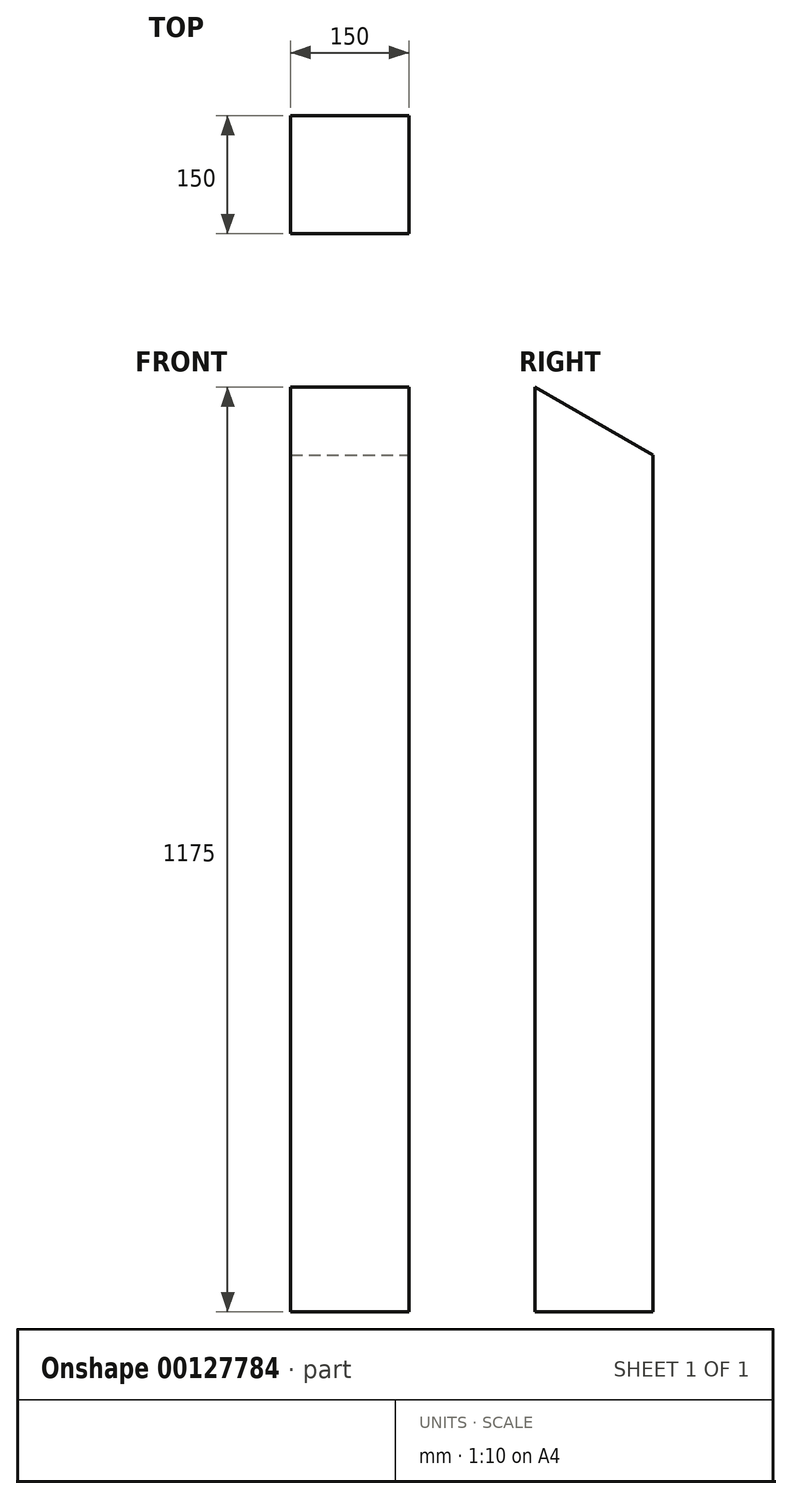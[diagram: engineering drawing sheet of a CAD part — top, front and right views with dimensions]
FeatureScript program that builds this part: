
annotation { "Feature Type Name" : "Feature", "Feature Type Description" : "" }
export const myFeature = defineFeature(function(context is Context, id is Id, definition is map)
    precondition{}
    {
        {
            var Q0;
            Q0=qCreatedBy(makeId("Top.planeOp"),FACE);
            var sketch = newSketch(context, id + "F0", { "sketchPlane" : qUnion([Q0])});
            skLineSegment(sketch, "E0.bottom", {"start": v(-75, 75) * mm, "end": v(75, 75) * mm});
            skLineSegment(sketch, "E0.top", {"start": v(-75, -75) * mm, "end": v(75, -75) * mm});
            skLineSegment(sketch, "E0.left", {"start": v(-75, 75) * mm, "end": v(-75, -75) * mm});
            skLineSegment(sketch, "E0.right", {"start": v(75, 75) * mm, "end": v(75, -75) * mm});
            skPoint(sketch, "E0.middle", {"position": v(0, 0) * mm});
            skSolve(sketch);
        }
        {
            var Q0;
            Q0 = qSketchRegion(id + "F0", true);
            extrude(context, id + "F1", {"entities" : qUnion([Q0]), "endBound" : BoundingType.SYMMETRIC, "depth" : 1175 * mm});
        }
        {
            var Q0;
            Q0=makeQuery(id+"F1.opExtrude","SWEPT_FACE",FACE,{"disambiguationData":[OSD([sQuery(id+"F0.wireOp",EDGE,"E0.right")])]});
            var sketch = newSketch(context, id + "F2", { "sketchPlane" : qUnion([Q0])});
            skLineSegment(sketch, "E1", {"start": v(-75, 587.5) * mm, "end": v(75, 500.9) * mm});
            skLineSegment(sketch, "E2", {"start": v(75, 500.9) * mm, "end": v(75, 587.5) * mm});
            skLineSegment(sketch, "E3", {"start": v(75, 587.5) * mm, "end": v(-75, 587.5) * mm});
            skSolve(sketch);
        }
        {
            var Q0;
            Q0 = qSketchRegion(id + "F2", true);
            extrude(context, id + "F3", {"entities" : qUnion([Q0]), "operationType" : NewBodyOperationType.REMOVE, "endBound" : BoundingType.UP_TO_NEXT, "oppositeDirection" : true, "depth" : 25 * mm});
        }
    });
